# Revit family: NBS_Senator_OffcTbls_Array_Rectangular600mm
name_source: partatom
category: Furniture
revit_build: Autodesk Revit 2018 (Build: 20190510_1515(x64)
units: mm (PartAtom-declared; Revit-internal decimal feet)

## family parameters
Always vertical = Yes
Cut with Voids When Loaded = No
Room Calculation Point = No
Shared = No
Work Plane-Based = No

## types (5) — shared parameters
Application = Office and educational settings
AssetType = Fixed
Category = Pr_40_50_21_60:Office tables
CodePerformance = BS EN 15372, BS EN 6396
Color = Silver, white, black
Description = Rectangle table
DurationUnit = year
Features = Rigid cast aluminium frame, fully integrated cable management, lockable brake castors, nesting capabilities, gas assisted lift, single hand to unlock, flexible swipe-in cable risers, 25 mm MFC tops
Finish = Highland oak, beech, maple, white, autumn, winter oak, strata oak, mocha, carini walnutm hacienda white, denim, clay, lemon sorbet, light grey
IfcExportAs = IfcFurnitureType
IfcExportType = TABLE
IsBuiltIn = No
ManufacturerName = The Senator Group
ManufacturerURL = www.senator.co.uk
Material = Aluminium, wood
NBSCertification = www.nationalbimlibrary.com/cert/yyuc5f0r
NBSDescription = Office tables
NBSReference = 45-35-20/340
NominalDepth = 600 mm  [stored 1.9685 ft]
OptionalExtras = Below desk power complete with flip unit, in-surface power unit, flip in-surface power unit
ProductInformation = http://www.thesenatorgroup.com
SpecifiableFeatures = Quadrants, modesty panels, aluminium cable riser
Status = UNSET
Style = Table
TableDepth = 600 mm  [stored 1.9685 ft]
TableHeight = 740 mm  [stored 2.42782 ft]
TableTopMaterial = NBS_Senator_Wood_Dark_Mocha
Uniclass2015Code = Pr_40_50_21_60
Uniclass2015Title = Office tables
Uniclass2015Version = Products v1.16
Version = 1
WarrantyDurationUnit = year
zero-valued in all types: NumberOfChairs, WorksurfaceArea

## per-type parameters (varying)
| type | BIMObjectName | ExpectedLife | FrameMaterial | InternalWheelMatrial | ModelNumber | Name | NominalHeight | NominalLength | NominalWidth | Size | SustainabilityPerformance | TableTopThickness | TableWidth | WarrantyDescription | WarrantyDurationParts | WheelBrakeMaterial | WheelMaterial |
| Array-Rectangular600mm_ARC1206RC | NBS_The Senator Group_OfficeTables_Array-Rectangular600mm_ARC1206RC | 15 | NBS_SenatorGroup_Aluminium_Rigid_Siver | NBS_SenatorGroup_Aluminium_Flat_Silver | ARC1206RC | OfficeTables_Array-Rectangular600mm_ARC1206RC_TheSenatorGroup | 740 mm  [stored 2.42782 ft] | 1200 mm | 1200 mm | 600 x 1200 mm | 99% recyclable | 25 mm | 1200 mm | Senator warrants that its manufactured products are free from manufacturing defects - in materials or workmanship - for a period of ten (10) years on Senator Seating ranges; and fifteen (15) years on Senator Desking ranges - exceptions are listed below. Senator will repair or replace (at Senator’s sole discretion) with comparable free of charge materials / components, any product / component, which fails under normal use in a single shift environment, as a result of a defect in the materials and / or workmanship. | 15 | NBS_SenatorGroup_Plastic_Grey | NBS_SenatorGroup_Rubber_Black |
| Array-Rectangular600mm_ARC1406RC | NBS_The Senator Group_OfficeTables_Array-Rectangular600mm_ARC1406RC | 15 | NBS_Senator_Aluminium_Rigid_Siver | NBS_Senator_Aluminium_Flat_Silver | ARC1406RC | OfficeTables_Array-Rectangular600mm_ARC1406RC_TheSenatorGroup | 740 mm  [stored 2.42782 ft] | 1400 mm  [stored 4.59318 ft] | 1400 mm  [stored 4.59318 ft] | 600 x 1400 mm | 99% recyclable | 25 mm | 1400 mm  [stored 4.59318 ft] | Senator warrants that its manufactured products are free from manufacturing defects - in materials or workmanship - for a period of ten (10) years on Senator Seating ranges; and fifteen (15) years on Senator Desking ranges - exceptions are listed below. Senator will repair or replace (at Senator’s sole discretion) with comparable free of charge materials / components, any product / component, which fails under normal use in a single shift environment, as a result of a defect in the materials and / or workmanship. | 15 | NBS_Senator_Plastic_Grey | NBS_Senator_Rubber_Black |
| Array-Rectangular600mm_ARC1506RC | NBS_The Senator Group_OfficeTables_Array-Rectangular600mm_ARC1506RC | 15 | NBS_Senator_Aluminium_Rigid_Siver | NBS_Senator_Aluminium_Flat_Silver | ARC1506RC | OfficeTables_Array-Rectangular600mm_ARC1506RC_TheSenatorGroup | 740 mm  [stored 2.42782 ft] | 1500 mm  [stored 4.92126 ft] | 1500 mm  [stored 4.92126 ft] | 600 x 1500 mm | 99% recyclable | 25 mm | 1500 mm  [stored 4.92126 ft] | Senator warrants that its manufactured products are free from manufacturing defects - in materials or workmanship - for a period of ten (10) years on Senator Seating ranges; and fifteen (15) years on Senator Desking ranges - exceptions are listed below. Senator will repair or replace (at Senator’s sole discretion) with comparable free of charge materials / components, any product / component
which fails under normal use in a single shift environment, as a result of a defect in the materials and / or workmanship. | 15 | NBS_Senator_Plastic_Grey | NBS_Senator_Rubber_Black |
| Array-Rectangular600mm_ARC1606RC | NBS_The Senator Group_OfficeTables_Array-Rectangular600mm_ARC1606RC |  | NBS_Senator_Aluminium_Rigid_Siver | NBS_Senator_Aluminium_Flat_Silver | ARC1606RC | OfficeTables_Array-Rectangular600mm_ARC1606RC_TheSenatorGroup | 0 mm  [stored 0 ft] | 0 mm  [stored 0 ft] | 1600 mm  [stored 5.24934 ft] | 600 x 1600 mm |  | 2 mm | 1600 mm  [stored 5.24934 ft] |  |  | NBS_Senator_Plastic_Grey | NBS_Senator_Rubber_Black |
| Array-Rectangular600mm_ARC1806RC | NBS_TheSenatorGroup_OfficeTables_Array-Rectangular600mm_ARC1806RC |  | NBS_Senator_Aluminium_Rigid_Siver | NBS_Senator_Aluminium_Flat_Silver | ARC1806RC | OfficeTables_Array-Rectangular600mm_ARC1806RC_TheSenatorGroup | 0 mm  [stored 0 ft] | 0 mm  [stored 0 ft] | 1800 mm  [stored 5.90551 ft] | 600 x 1800 mm |  | 2 mm | 1800 mm  [stored 5.90551 ft] |  |  | NBS_Senator_Plastic_Grey | NBS_Senator_Rubber_Black |

note: column(s) folded — value = type name in every type: ModelReference

note: [stored X ft] marks values corroborated as IEEE doubles in the binary element streams (Revit-internal decimal feet)

## geometry (parser evidence)
native form markers: Sweep x8
no freeform markers — native parametric forms only
